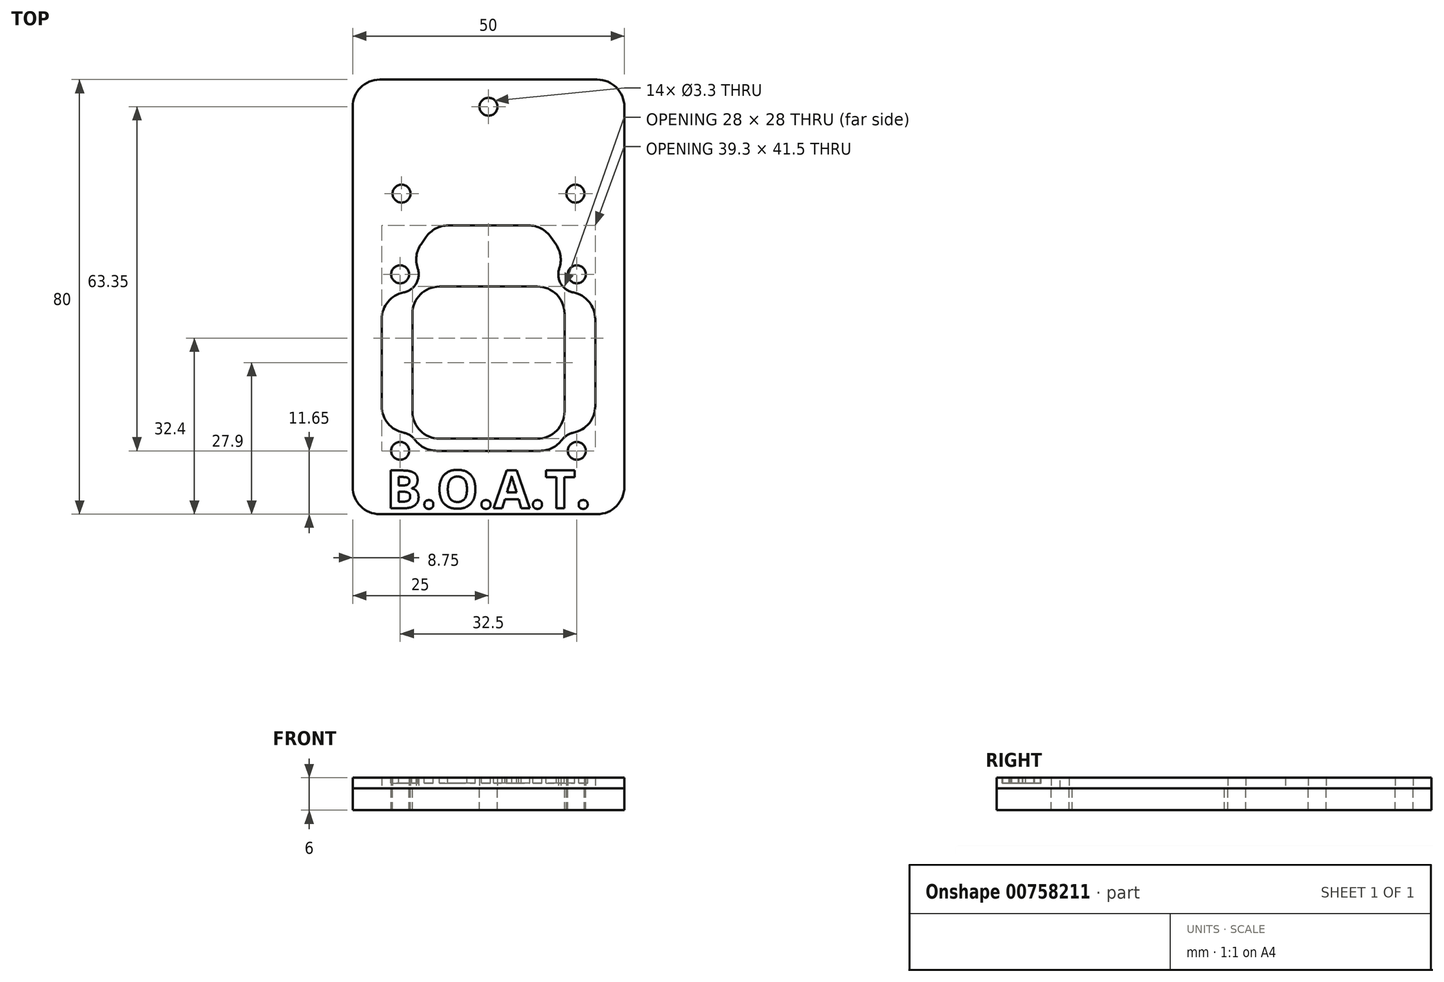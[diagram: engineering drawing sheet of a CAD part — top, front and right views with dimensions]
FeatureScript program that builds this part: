
annotation { "Feature Type Name" : "Feature", "Feature Type Description" : "" }
export const myFeature = defineFeature(function(context is Context, id is Id, definition is map)
    precondition{}
    {
        {
            var Q0;
            Q0=qCreatedBy(makeId("Top.planeOp"),FACE);
            var sketch = newSketch(context, id + "F0", { "sketchPlane" : qUnion([Q0])});
            skLineSegment(sketch, "E0.bottom", {"start": v(25, 0) * mm, "end": v(-25, 0) * mm});
            skLineSegment(sketch, "E0.top", {"start": v(25, 26) * mm, "end": v(-25, 26) * mm});
            skLineSegment(sketch, "E0.left", {"start": v(25, 0) * mm, "end": v(25, 26) * mm});
            skLineSegment(sketch, "E0.right", {"start": v(-25, 0) * mm, "end": v(-25, 26) * mm});
            skPoint(sketch, "E0.middle", {"position": v(0, 13) * mm});
            skLineSegment(sketch, "E1.bottom", {"start": v(25, -54) * mm, "end": v(-25, -54) * mm});
            skLineSegment(sketch, "E1.left", {"start": v(25, -54) * mm, "end": v(25, 0) * mm});
            skLineSegment(sketch, "E1.right", {"start": v(-25, -54) * mm, "end": v(-25, 0) * mm});
            skPoint(sketch, "E1.middle", {"position": v(0, -27) * mm});
            skSolve(sketch);
        }
        {
            var Q0;
            Q0=qCreatedBy(makeId("Top.planeOp"),FACE);
            var sketch = newSketch(context, id + "F1", { "sketchPlane" : qUnion([Q0])});
            skCircle(sketch, "E2", {"center": v(0, 21) * mm, "radius": 1.65 * mm});
            skCircle(sketch, "E3", {"center": v(-16, 5) * mm, "radius": 1.65 * mm});
            skCircle(sketch, "E4", {"center": v(16, 5) * mm, "radius": 1.65 * mm});
            skSolve(sketch);
        }
        {
            var Q0;
            Q0=qCreatedBy(makeId("Top.planeOp"),FACE);
            var sketch = newSketch(context, id + "F2", { "sketchPlane" : qUnion([Q0])});
            skCircle(sketch, "E5", {"center": v(16.25, -9.85) * mm, "radius": 1.65 * mm});
            skCircle(sketch, "E6", {"center": v(-16.25, -9.85) * mm, "radius": 1.65 * mm});
            skCircle(sketch, "E7", {"center": v(-16.25, -42.35) * mm, "radius": 1.65 * mm});
            skCircle(sketch, "E8", {"center": v(16.25, -42.35) * mm, "radius": 1.65 * mm});
            skPoint(sketch, "E9", {"position": v(0, -26.1) * mm});
            skSolve(sketch);
        }
        {
            var Q0;
            Q0=qCreatedBy(makeId("Top.planeOp"),FACE);
            var sketch = newSketch(context, id + "F3", { "sketchPlane" : qUnion([Q0])});
            skLineSegment(sketch, "E10.bottom", {"start": v(14, -40.1) * mm, "end": v(-14, -40.1) * mm});
            skLineSegment(sketch, "E10.top", {"start": v(14, -12.1) * mm, "end": v(-14, -12.1) * mm});
            skLineSegment(sketch, "E10.left", {"start": v(14, -40.1) * mm, "end": v(14, -12.1) * mm});
            skLineSegment(sketch, "E10.right", {"start": v(-14, -40.1) * mm, "end": v(-14, -12.1) * mm});
            skPoint(sketch, "E10.middle", {"position": v(0, -26.1) * mm});
            skSolve(sketch);
        }
        {
            var Q0;
            Q0=qCreatedBy(makeId("Top.planeOp"),FACE);
            var sketch = newSketch(context, id + "F4", { "sketchPlane" : qUnion([Q0])});
            skCircle(sketch, "E11", {"center": v(-16.25, -9.85) * mm, "radius": 3.4 * mm});
            skCircle(sketch, "E12", {"center": v(16.25, -9.85) * mm, "radius": 3.4 * mm});
            skCircle(sketch, "E13", {"center": v(-16.25, -42.35) * mm, "radius": 3.4 * mm});
            skCircle(sketch, "E14", {"center": v(16.25, -42.35) * mm, "radius": 3.4 * mm});
            skLineSegment(sketch, "E15", {"start": v(16.25, -42.35) * mm, "end": v(-16.25, -42.35) * mm});
            skPoint(sketch, "E16", {"position": v(0, -0.85) * mm});
            skLineSegment(sketch, "E17", {"start": v(-7.38, -0.85) * mm, "end": v(7.38, -0.85) * mm});
            skLineSegment(sketch, "E18", {"start": v(-16.25, -9.85) * mm, "end": v(-11.5, -3) * mm});
            skLineSegment(sketch, "E19", {"start": v(11.5, -3) * mm, "end": v(16.25, -9.85) * mm});
            skPoint(sketch, "E20.visualSharp", {"position": v(-10, -0.85) * mm});
            skArc(sketch, "E20.filletArc", {"start": v(-7.38, -0.85) * mm, "mid": v(-9.7, -1.42) * mm, "end": v(-11.5, -3) * mm});
            skPoint(sketch, "E21.visualSharp", {"position": v(10, -0.85) * mm});
            skArc(sketch, "E21.filletArc", {"start": v(11.5, -3) * mm, "mid": v(9.7, -1.42) * mm, "end": v(7.38, -0.85) * mm});
            skPoint(sketch, "E22", {"position": v(-19.65, -9.85) * mm});
            skPoint(sketch, "E23", {"position": v(-19.65, -42.35) * mm});
            skPoint(sketch, "E24", {"position": v(19.65, -42.35) * mm});
            skPoint(sketch, "E25", {"position": v(19.65, -9.85) * mm});
            skLineSegment(sketch, "E26", {"start": v(-19.65, -9.85) * mm, "end": v(-19.65, -42.35) * mm});
            skLineSegment(sketch, "E27", {"start": v(19.65, -42.35) * mm, "end": v(19.65, -9.85) * mm});
            skSolve(sketch);
        }
        {
            assignVariable(context, id + "F5", {"name" : "topthk", "anyValue" : 2});
        }
        {
            var Q0;
            Q0=makeQuery(id+"F0.imprint","IMPRINT",FACE,{"disambiguationData":[TD([[makeQuery(id+"F0.imprint","IMPRINT",EDGE,{"derivedFrom":sQuery(id+"F0.wireOp",EDGE,"E0.top")}),1.0]])]});
            var Q1;
            Q1=makeQuery(id+"F0.imprint","IMPRINT",FACE,{"disambiguationData":[TD([[makeQuery(id+"F0.imprint","IMPRINT",EDGE,{"derivedFrom":sQuery(id+"F0.wireOp",EDGE,"E1.bottom")}),-1.0]])]});
            extrude(context, id + "F6", {"entities" : qUnion([Q0, Q1]), "depth" : (getVariable(context, 'topthk')) * mm, "offsetDistance" : 25 * mm});
        }
        {
            var Q0;
            Q0=makeQuery(id+"F1.imprint","IMPRINT",FACE,{"disambiguationData":[TD([[makeQuery(id+"F1.imprint","IMPRINT",EDGE,{"derivedFrom":sQuery(id+"F1.wireOp",EDGE,"E2")}),1.0]])]});
            var Q1;
            Q1=makeQuery(id+"F1.imprint","IMPRINT",FACE,{"disambiguationData":[TD([[makeQuery(id+"F1.imprint","IMPRINT",EDGE,{"derivedFrom":sQuery(id+"F1.wireOp",EDGE,"E4")}),1.0]])]});
            var Q2;
            Q2=makeQuery(id+"F1.imprint","IMPRINT",FACE,{"disambiguationData":[TD([[makeQuery(id+"F1.imprint","IMPRINT",EDGE,{"derivedFrom":sQuery(id+"F1.wireOp",EDGE,"E3")}),1.0]])]});
            var Q3;
            {var subQ3=sQuery(id+"F4.wireOp",EDGE,"VfGTtrIR-PoAK-8kTx-iHd4-9SxL4KJkVbjK");var subQ5=sQuery(id+"F4.wireOp",EDGE,"E11");var subQ6=makeQuery(id+"F4.imprint","INTERSECT",VERTEX,{"derivedFrom":[subQ5,subQ3]});Q3=makeQuery(id+"F4.imprint","IMPRINT",FACE,{"disambiguationData":[TD([[makeQuery(id+"F4.imprint","IMPRINT",EDGE,{"disambiguationData":[TD([[subQ6,-1.0]])],"derivedFrom":subQ5}),-1.0]])]});}
            var Q4;
            Q4=makeQuery(id+"F2.imprint","IMPRINT",FACE,{"disambiguationData":[TD([[makeQuery(id+"F2.imprint","IMPRINT",EDGE,{"derivedFrom":sQuery(id+"F2.wireOp",EDGE,"E8")}),1.0]])]});
            var Q5;
            Q5=makeQuery(id+"F2.imprint","IMPRINT",FACE,{"disambiguationData":[TD([[makeQuery(id+"F2.imprint","IMPRINT",EDGE,{"derivedFrom":sQuery(id+"F2.wireOp",EDGE,"E7")}),1.0]])]});
            extrude(context, id + "F7", {"entities" : qUnion([Q0, Q1, Q2, Q3, Q4, Q5]), "operationType" : NewBodyOperationType.REMOVE, "depth" : (getVariable(context, 'topthk')) * mm, "offsetDistance" : 25 * mm});
        }
        {
            var Q0;
            Q0=makeQuery(id+"F2.imprint","IMPRINT",FACE,{"disambiguationData":[TD([[makeQuery(id+"F2.imprint","IMPRINT",EDGE,{"derivedFrom":sQuery(id+"F2.wireOp",EDGE,"E6")}),1.0]])]});
            var Q1;
            Q1=makeQuery(id+"F2.imprint","IMPRINT",FACE,{"disambiguationData":[TD([[makeQuery(id+"F2.imprint","IMPRINT",EDGE,{"derivedFrom":sQuery(id+"F2.wireOp",EDGE,"E5")}),1.0]])]});
            extrude(context, id + "F8", {"entities" : qUnion([Q0, Q1]), "operationType" : NewBodyOperationType.REMOVE, "depth" : (getVariable(context, 'topthk')) * mm, "offsetDistance" : 25 * mm});
        }
        {
            var Q0;
            Q0=makeQuery(id+"F6.opExtrude","CAP_FACE",FACE,{"disambiguationData":[OSD([sQuery(id+"F0.wireOp",EDGE,"E0.top"),sQuery(id+"F0.wireOp",EDGE,"E0.left"),sQuery(id+"F0.wireOp",EDGE,"E0.right"),sQuery(id+"F0.wireOp",EDGE,"E1.bottom"),sQuery(id+"F0.wireOp",EDGE,"E1.left"),sQuery(id+"F0.wireOp",EDGE,"E1.right")])],"isStart":false});
            var sketch = newSketch(context, id + "F9", { "sketchPlane" : qUnion([Q0])});
            skText(sketch, "E28", { "text": "B.O.A.T.", "fontName": "OpenSans-Bold.ttf"});
            const initialGuessF9  = {"E28": [-0.01889, -0.0529, 1, 0, 0.007]};
            skSetInitialGuess(sketch, initialGuessF9);
            skSolve(sketch);
        }
        {
            var Q0;
            Q0 = qSketchRegion(id + "F9", true);
            extrude(context, id + "F10", {"entities" : qUnion([Q0]), "operationType" : NewBodyOperationType.REMOVE, "oppositeDirection" : true, "depth" : 1 * mm, "offsetDistance" : 25 * mm});
        }
        {
            assignVariable(context, id + "F11", {"name" : "botthk", "anyValue" : 4});
        }
        {
            var Q0;
            Q0=makeQuery(id+"F0.imprint","IMPRINT",FACE,{"disambiguationData":[TD([[makeQuery(id+"F0.imprint","IMPRINT",EDGE,{"derivedFrom":sQuery(id+"F0.wireOp",EDGE,"E1.bottom")}),-1.0]])]});
            var Q1;
            Q1=makeQuery(id+"F0.imprint","IMPRINT",FACE,{"disambiguationData":[TD([[makeQuery(id+"F0.imprint","IMPRINT",EDGE,{"derivedFrom":sQuery(id+"F0.wireOp",EDGE,"E0.top")}),1.0]])]});
            extrude(context, id + "F12", {"entities" : qUnion([Q0, Q1]), "oppositeDirection" : true, "depth" : (getVariable(context, 'botthk')) * mm, "offsetDistance" : 25 * mm});
        }
        {
            var Q0;
            Q0=makeQuery(id+"F1.imprint","IMPRINT",FACE,{"disambiguationData":[TD([[makeQuery(id+"F1.imprint","IMPRINT",EDGE,{"derivedFrom":sQuery(id+"F1.wireOp",EDGE,"E3")}),1.0]])]});
            var Q1;
            Q1=makeQuery(id+"F1.imprint","IMPRINT",FACE,{"disambiguationData":[TD([[makeQuery(id+"F1.imprint","IMPRINT",EDGE,{"derivedFrom":sQuery(id+"F1.wireOp",EDGE,"E2")}),1.0]])]});
            var Q2;
            Q2=makeQuery(id+"F1.imprint","IMPRINT",FACE,{"disambiguationData":[TD([[makeQuery(id+"F1.imprint","IMPRINT",EDGE,{"derivedFrom":sQuery(id+"F1.wireOp",EDGE,"E4")}),1.0]])]});
            var Q3;
            Q3=makeQuery(id+"F2.imprint","IMPRINT",FACE,{"disambiguationData":[TD([[makeQuery(id+"F2.imprint","IMPRINT",EDGE,{"derivedFrom":sQuery(id+"F2.wireOp",EDGE,"E5")}),1.0]])]});
            var Q4;
            Q4=makeQuery(id+"F2.imprint","IMPRINT",FACE,{"disambiguationData":[TD([[makeQuery(id+"F2.imprint","IMPRINT",EDGE,{"derivedFrom":sQuery(id+"F2.wireOp",EDGE,"E6")}),1.0]])]});
            var Q5;
            Q5=makeQuery(id+"F2.imprint","IMPRINT",FACE,{"disambiguationData":[TD([[makeQuery(id+"F2.imprint","IMPRINT",EDGE,{"derivedFrom":sQuery(id+"F2.wireOp",EDGE,"E7")}),1.0]])]});
            var Q6;
            Q6=makeQuery(id+"F2.imprint","IMPRINT",FACE,{"disambiguationData":[TD([[makeQuery(id+"F2.imprint","IMPRINT",EDGE,{"derivedFrom":sQuery(id+"F2.wireOp",EDGE,"E8")}),1.0]])]});
            var Q7;
            Q7=makeQuery(id+"F3.imprint","IMPRINT",FACE,{"disambiguationData":[TD([[makeQuery(id+"F3.imprint","IMPRINT",EDGE,{"derivedFrom":sQuery(id+"F3.wireOp",EDGE,"E10.bottom")}),-1.0]])]});
            extrude(context, id + "F13", {"entities" : qUnion([Q0, Q1, Q2, Q3, Q4, Q5, Q6, Q7]), "operationType" : NewBodyOperationType.REMOVE, "oppositeDirection" : true, "depth" : (getVariable(context, 'botthk')) * mm, "offsetDistance" : 25 * mm});
        }
        {
            var Q0;
            Q0=makeQuery(id+"F6.opExtrude","SWEPT_EDGE",EDGE,{"disambiguationData":[OSD([sQuery(id+"F0.wireOp",EDGE,"E1.bottom"),sQuery(id+"F0.wireOp",EDGE,"E1.left")])]});
            var Q1;
            Q1=makeQuery(id+"F12.opExtrude","SWEPT_EDGE",EDGE,{"disambiguationData":[OSD([sQuery(id+"F0.wireOp",EDGE,"E1.bottom"),sQuery(id+"F0.wireOp",EDGE,"E1.left")])]});
            var Q2;
            Q2=makeQuery(id+"F6.opExtrude","SWEPT_EDGE",EDGE,{"disambiguationData":[OSD([sQuery(id+"F0.wireOp",EDGE,"E0.top"),sQuery(id+"F0.wireOp",EDGE,"E0.left")])]});
            var Q3;
            Q3=makeQuery(id+"F12.opExtrude","SWEPT_EDGE",EDGE,{"disambiguationData":[OSD([sQuery(id+"F0.wireOp",EDGE,"E0.top"),sQuery(id+"F0.wireOp",EDGE,"E0.left")])]});
            var Q4;
            Q4=makeQuery(id+"F12.opExtrude","SWEPT_EDGE",EDGE,{"disambiguationData":[OSD([sQuery(id+"F0.wireOp",EDGE,"E0.top"),sQuery(id+"F0.wireOp",EDGE,"E0.right")])]});
            var Q5;
            Q5=makeQuery(id+"F6.opExtrude","SWEPT_EDGE",EDGE,{"disambiguationData":[OSD([sQuery(id+"F0.wireOp",EDGE,"E0.top"),sQuery(id+"F0.wireOp",EDGE,"E0.right")])]});
            var Q6;
            Q6=makeQuery(id+"F6.opExtrude","SWEPT_EDGE",EDGE,{"disambiguationData":[OSD([sQuery(id+"F0.wireOp",EDGE,"E1.bottom"),sQuery(id+"F0.wireOp",EDGE,"E1.right")])]});
            var Q7;
            Q7=makeQuery(id+"F12.opExtrude","SWEPT_EDGE",EDGE,{"disambiguationData":[OSD([sQuery(id+"F0.wireOp",EDGE,"E1.bottom"),sQuery(id+"F0.wireOp",EDGE,"E1.right")])]});
            fillet(context, id + "F14", {"entities" : qUnion([Q0, Q1, Q2, Q3, Q4, Q5, Q6, Q7]), "radius" : 5 * mm, "tangentPropagation" : true, "allowEdgeOverflow" : false});
        }
        {
            var Q0;
            Q0=makeQuery(id+"F7.boolean.opBoolean","COPY",EDGE,{"derivedFrom":makeQuery(id+"F7.opExtrude","SWEPT_EDGE",EDGE,{"disambiguationData":[OSD([sQuery(id+"F4.wireOp",EDGE,"E11"),sQuery(id+"F4.wireOp",EDGE,"VfGTtrIR-PoAK-8kTx-iHd4-9SxL4KJkVbjK")])]})});
            var Q1;
            Q1=makeQuery(id+"F7.boolean.opBoolean","COPY",EDGE,{"derivedFrom":makeQuery(id+"F7.opExtrude","SWEPT_EDGE",EDGE,{"disambiguationData":[OSD([sQuery(id+"F4.wireOp",EDGE,"E12"),sQuery(id+"F4.wireOp",EDGE,"nbDYn37d-xDA6-RIb9-SW6W-Bcq0SxFR7eAV")])]})});
            var Q2;
            Q2=makeQuery(id+"F7.boolean.opBoolean","COPY",EDGE,{"derivedFrom":makeQuery(id+"F7.opExtrude","SWEPT_EDGE",EDGE,{"disambiguationData":[OSD([sQuery(id+"F4.wireOp",EDGE,"E14"),sQuery(id+"F4.wireOp",EDGE,"nbDYn37d-xDA6-RIb9-SW6W-Bcq0SxFR7eAV")])]})});
            var Q3;
            Q3=makeQuery(id+"F7.boolean.opBoolean","COPY",EDGE,{"derivedFrom":makeQuery(id+"F7.opExtrude","SWEPT_EDGE",EDGE,{"disambiguationData":[OSD([sQuery(id+"F4.wireOp",EDGE,"E14"),sQuery(id+"F4.wireOp",EDGE,"E15")])]})});
            var Q4;
            Q4=makeQuery(id+"F7.boolean.opBoolean","COPY",EDGE,{"derivedFrom":makeQuery(id+"F7.opExtrude","SWEPT_EDGE",EDGE,{"disambiguationData":[OSD([sQuery(id+"F4.wireOp",EDGE,"E13"),sQuery(id+"F4.wireOp",EDGE,"E15")])]})});
            var Q5;
            Q5=makeQuery(id+"F7.boolean.opBoolean","COPY",EDGE,{"derivedFrom":makeQuery(id+"F7.opExtrude","SWEPT_EDGE",EDGE,{"disambiguationData":[OSD([sQuery(id+"F4.wireOp",EDGE,"E13"),sQuery(id+"F4.wireOp",EDGE,"VfGTtrIR-PoAK-8kTx-iHd4-9SxL4KJkVbjK")])]})});
            var Q6;
            Q6=makeQuery(id+"F7.boolean.opBoolean","COPY",EDGE,{"derivedFrom":makeQuery(id+"F7.opExtrude","SWEPT_EDGE",EDGE,{"disambiguationData":[OSD([sQuery(id+"F4.wireOp",EDGE,"E12"),sQuery(id+"F4.wireOp",EDGE,"E19")])]})});
            var Q7;
            Q7=makeQuery(id+"F7.boolean.opBoolean","COPY",EDGE,{"derivedFrom":makeQuery(id+"F7.opExtrude","SWEPT_EDGE",EDGE,{"disambiguationData":[OSD([sQuery(id+"F4.wireOp",EDGE,"E11"),sQuery(id+"F4.wireOp",EDGE,"E18")])]})});
            var Q8;
            Q8=makeQuery(id+"F13.boolean.opBoolean","COPY",EDGE,{"derivedFrom":makeQuery(id+"F13.opExtrude","SWEPT_EDGE",EDGE,{"disambiguationData":[OSD([sQuery(id+"F3.wireOp",EDGE,"E10.top"),sQuery(id+"F3.wireOp",EDGE,"E10.right")])]})});
            var Q9;
            Q9=makeQuery(id+"F13.boolean.opBoolean","COPY",EDGE,{"derivedFrom":makeQuery(id+"F13.opExtrude","SWEPT_EDGE",EDGE,{"disambiguationData":[OSD([sQuery(id+"F3.wireOp",EDGE,"E10.top"),sQuery(id+"F3.wireOp",EDGE,"E10.left")])]})});
            var Q10;
            Q10=makeQuery(id+"F13.boolean.opBoolean","COPY",EDGE,{"derivedFrom":makeQuery(id+"F13.opExtrude","SWEPT_EDGE",EDGE,{"disambiguationData":[OSD([sQuery(id+"F3.wireOp",EDGE,"E10.bottom"),sQuery(id+"F3.wireOp",EDGE,"E10.left")])]})});
            var Q11;
            Q11=makeQuery(id+"F13.boolean.opBoolean","COPY",EDGE,{"derivedFrom":makeQuery(id+"F13.opExtrude","SWEPT_EDGE",EDGE,{"disambiguationData":[OSD([sQuery(id+"F3.wireOp",EDGE,"E10.bottom"),sQuery(id+"F3.wireOp",EDGE,"E10.right")])]})});
            fillet(context, id + "F15", {"entities" : qUnion([Q0, Q1, Q2, Q3, Q4, Q5, Q6, Q7, Q8, Q9, Q10, Q11]), "radius" : 5 * mm, "tangentPropagation" : true, "allowEdgeOverflow" : false});
        }
    });
